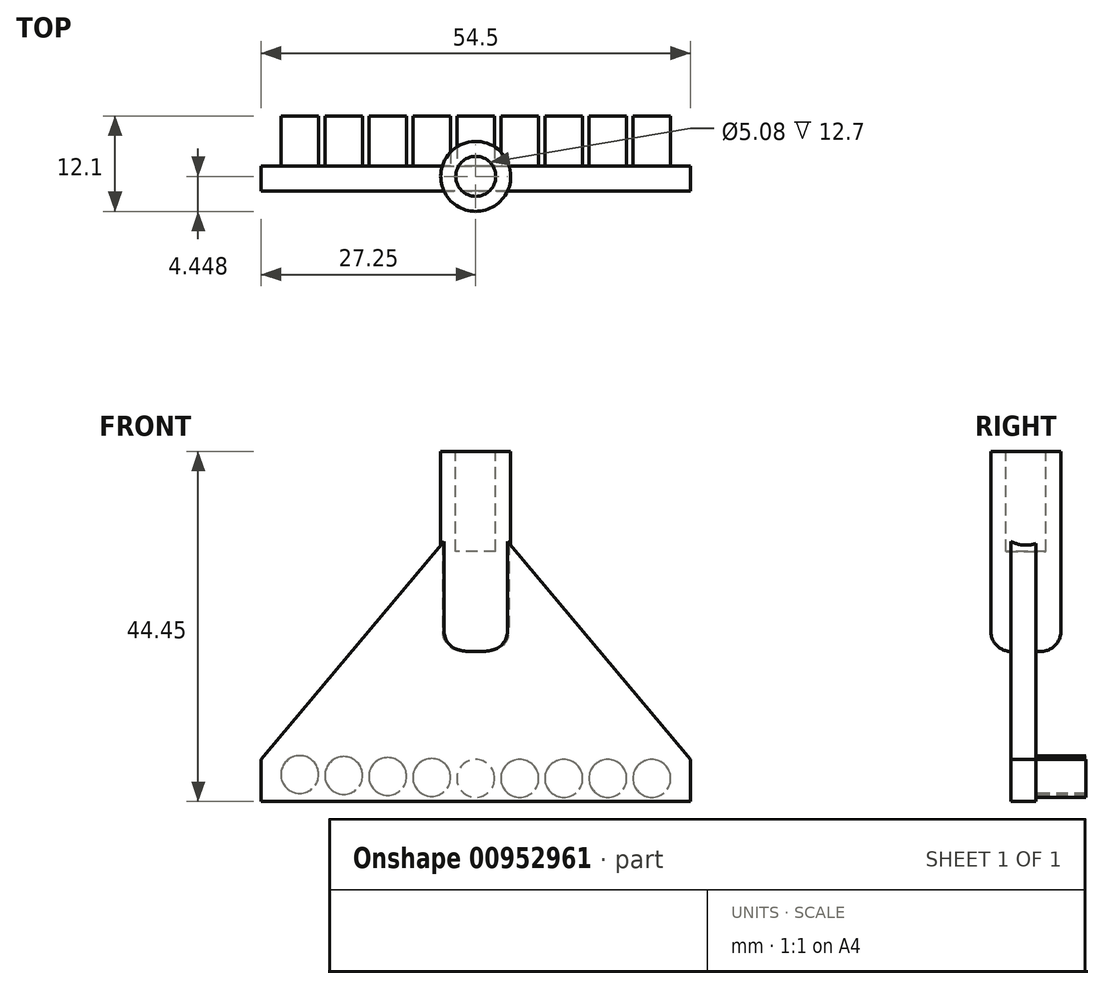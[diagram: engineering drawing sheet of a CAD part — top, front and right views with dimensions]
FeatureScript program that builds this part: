
annotation { "Feature Type Name" : "Feature", "Feature Type Description" : "" }
export const myFeature = defineFeature(function(context is Context, id is Id, definition is map)
    precondition{}
    {
        {
            var Q0;
            Q0=qCreatedBy(makeId("Front.planeOp"),FACE);
            var sketch = newSketch(context, id + "F0", { "sketchPlane" : qUnion([Q0])});
            skLineSegment(sketch, "E0", {"start": v(0, 37.84) * mm, "end": v(-27.25, 5.36) * mm});
            skLineSegment(sketch, "E1", {"start": v(-27.25, 0) * mm, "end": v(27.25, 0) * mm});
            skLineSegment(sketch, "E2", {"start": v(27.25, 5.36) * mm, "end": v(0, 37.84) * mm});
            skLineSegment(sketch, "E3", {"start": v(27.25, 5.36) * mm, "end": v(27.25, 0) * mm});
            skLineSegment(sketch, "E4.MirrorCS", {"start": v(-27.25, 5.36) * mm, "end": v(-27.25, 0) * mm});
            skPoint(sketch, "E5.orphan", {"position": v(31.75, 0) * mm});
            skPoint(sketch, "E6.orphan", {"position": v(-31.75, 0) * mm});
            skSolve(sketch);
        }
        {
            var Q0;
            Q0=makeQuery(id+"F0.imprint","IMPRINT",FACE,{"disambiguationData":[TD([[makeQuery(id+"F0.imprint","IMPRINT",EDGE,{"derivedFrom":sQuery(id+"F0.wireOp",EDGE,"E0")}),1.0]])]});
            extrude(context, id + "F1", {"entities" : qUnion([Q0]), "depth" : 3.17 * mm, "offsetDistance" : 25.4 * mm});
        }
        {
            var Q0;
            Q0=makeQuery(id+"F1.opExtrude","CAP_FACE",FACE,{"disambiguationData":[OSD([sQuery(id+"F0.wireOp",EDGE,"E0"),sQuery(id+"F0.wireOp",EDGE,"E1"),sQuery(id+"F0.wireOp",EDGE,"E2")])],"isStart":true});
            var sketch = newSketch(context, id + "F2", { "sketchPlane" : qUnion([Q0])});
            skCircle(sketch, "E7", {"center": v(0, 2.91) * mm, "radius": 2.4 * mm});
            skCircle(sketch, "E8.1.0.0", {"center": v(5.59, 3.04) * mm, "radius": 2.4 * mm});
            skCircle(sketch, "E8.2.0.0", {"center": v(11.18, 3.16) * mm, "radius": 2.4 * mm});
            skCircle(sketch, "E8.3.0.0", {"center": v(16.76, 3.28) * mm, "radius": 2.4 * mm});
            skCircle(sketch, "E8.4.0.0", {"center": v(22.35, 3.4) * mm, "radius": 2.4 * mm});
            skLineSegment(sketch, "E8.direction1", {"start": v(0, 2.91) * mm, "end": v(5.59, 3.04) * mm, "construction": true});
            skCircle(sketch, "E9.1.0.0", {"center": v(-5.59, 2.91) * mm, "radius": 2.4 * mm});
            skCircle(sketch, "E9.2.0.0", {"center": v(-11.18, 2.91) * mm, "radius": 2.4 * mm});
            skLineSegment(sketch, "E9.direction1", {"start": v(0, 2.91) * mm, "end": v(-5.59, 2.91) * mm, "construction": true});
            skCircle(sketch, "E10.0.3.0", {"center": v(-16.77, 2.91) * mm, "radius": 2.4 * mm});
            skCircle(sketch, "E10.0.4.0", {"center": v(-22.36, 2.91) * mm, "radius": 2.4 * mm});
            skSolve(sketch);
        }
        {
            var Q0;
            Q0=makeQuery(id+"F2.imprint","IMPRINT",FACE,{"disambiguationData":[TD([[makeQuery(id+"F2.imprint","IMPRINT",EDGE,{"derivedFrom":sQuery(id+"F2.wireOp",EDGE,"E8.3.0.0")}),1.0]])]});
            var Q1;
            Q1=makeQuery(id+"F2.imprint","IMPRINT",FACE,{"disambiguationData":[TD([[makeQuery(id+"F2.imprint","IMPRINT",EDGE,{"derivedFrom":sQuery(id+"F2.wireOp",EDGE,"E8.2.0.0")}),1.0]])]});
            var Q2;
            Q2=makeQuery(id+"F2.imprint","IMPRINT",FACE,{"disambiguationData":[TD([[makeQuery(id+"F2.imprint","IMPRINT",EDGE,{"derivedFrom":sQuery(id+"F2.wireOp",EDGE,"E8.1.0.0")}),1.0]])]});
            var Q3;
            Q3=makeQuery(id+"F2.imprint","IMPRINT",FACE,{"disambiguationData":[TD([[makeQuery(id+"F2.imprint","IMPRINT",EDGE,{"derivedFrom":sQuery(id+"F2.wireOp",EDGE,"E8.4.0.0")}),1.0]])]});
            var Q4;
            Q4=makeQuery(id+"F2.imprint","IMPRINT",FACE,{"disambiguationData":[TD([[makeQuery(id+"F2.imprint","IMPRINT",EDGE,{"derivedFrom":sQuery(id+"F2.wireOp",EDGE,"E7")}),1.0]])]});
            var Q5;
            Q5=makeQuery(id+"F2.imprint","IMPRINT",FACE,{"disambiguationData":[TD([[makeQuery(id+"F2.imprint","IMPRINT",EDGE,{"derivedFrom":sQuery(id+"F2.wireOp",EDGE,"E9.1.0.0")}),1.0]])]});
            var Q6;
            Q6=makeQuery(id+"F2.imprint","IMPRINT",FACE,{"disambiguationData":[TD([[makeQuery(id+"F2.imprint","IMPRINT",EDGE,{"derivedFrom":sQuery(id+"F2.wireOp",EDGE,"E9.2.0.0")}),1.0]])]});
            var Q7;
            Q7=makeQuery(id+"F2.imprint","IMPRINT",FACE,{"disambiguationData":[TD([[makeQuery(id+"F2.imprint","IMPRINT",EDGE,{"derivedFrom":sQuery(id+"F2.wireOp",EDGE,"E10.0.4.0")}),1.0]])]});
            var Q8;
            Q8=makeQuery(id+"F2.imprint","IMPRINT",FACE,{"disambiguationData":[TD([[makeQuery(id+"F2.imprint","IMPRINT",EDGE,{"derivedFrom":sQuery(id+"F2.wireOp",EDGE,"E10.0.3.0")}),1.0]])]});
            extrude(context, id + "F3", {"entities" : qUnion([Q0, Q1, Q2, Q3, Q4, Q5, Q6, Q7, Q8]), "operationType" : NewBodyOperationType.ADD, "depth" : 6.35 * mm, "offsetDistance" : 25.4 * mm});
        }
        {
            var Q0;
            Q0=qCreatedBy(makeId("Top.planeOp"),FACE);
            cPlane(context, id + "F4", {"entities" : qUnion([Q0]), "cplaneType" : CPlaneType.OFFSET, "offset" : 19.05 * mm, "width" : 152.4 * mm, "height" : 152.4 * mm});
        }
        {
            var Q0;
            Q0=qCreatedBy(id+"F4.planeOp",FACE);
            var sketch = newSketch(context, id + "F5", { "sketchPlane" : qUnion([Q0])});
            skCircle(sketch, "E11", {"center": v(0, -1.3) * mm, "radius": 4.45 * mm});
            skSolve(sketch);
        }
        {
            var Q0;
            Q0=makeQuery(id+"F5.imprint","IMPRINT",FACE,{"disambiguationData":[TD([[makeQuery(id+"F5.imprint","IMPRINT",EDGE,{"derivedFrom":sQuery(id+"F5.wireOp",EDGE,"E11")}),1.0]])]});
            extrude(context, id + "F6", {"entities" : qUnion([Q0]), "operationType" : NewBodyOperationType.ADD, "depth" : 25.4 * mm, "offsetDistance" : 25.4 * mm});
        }
        {
            var Q0;
            {var subQ0=sQuery(id+"F5.wireOp",EDGE,"E11");Q0=makeQuery(id+"F6.boolean.opBoolean","SPLIT",EDGE,{"disambiguationData":[TD([makeQuery(id+"F1.opExtrude","CAP_FACE",FACE,{"disambiguationData":[OSD([sQuery(id+"F0.wireOp",EDGE,"E0"),sQuery(id+"F0.wireOp",EDGE,"E1"),sQuery(id+"F0.wireOp",EDGE,"E2"),sQuery(id+"F0.wireOp",EDGE,"E3"),sQuery(id+"F0.wireOp",EDGE,"E4.MirrorCS")])],"isStart":true})])],"derivedFrom":makeQuery(id+"F6.opExtrude","CAP_EDGE",EDGE,{"disambiguationData":[OSD([subQ0])],"isStart":true})});}
            fillet(context, id + "F7", {"entities" : qUnion([Q0]), "radius" : 2.54 * mm, "allowEdgeOverflow" : false});
        }
        {
            var Q0;
            {var subQ0=sQuery(id+"F5.wireOp",EDGE,"E11");Q0=makeQuery(id+"F6.boolean.opBoolean","SPLIT",EDGE,{"disambiguationData":[TD([makeQuery(id+"F1.opExtrude","CAP_FACE",FACE,{"disambiguationData":[OSD([sQuery(id+"F0.wireOp",EDGE,"E0"),sQuery(id+"F0.wireOp",EDGE,"E1"),sQuery(id+"F0.wireOp",EDGE,"E2"),sQuery(id+"F0.wireOp",EDGE,"E3"),sQuery(id+"F0.wireOp",EDGE,"E4.MirrorCS")])],"isStart":false})])],"derivedFrom":makeQuery(id+"F6.opExtrude","CAP_EDGE",EDGE,{"disambiguationData":[OSD([subQ0])],"isStart":true})});}
            fillet(context, id + "F8", {"entities" : qUnion([Q0]), "radius" : 2.54 * mm, "allowEdgeOverflow" : false});
        }
        {
            var Q0;
            Q0=makeQuery(id+"F6.opExtrude","CAP_FACE",FACE,{"disambiguationData":[OSD([sQuery(id+"F5.wireOp",EDGE,"E11")])],"isStart":false});
            var sketch = newSketch(context, id + "F9", { "sketchPlane" : qUnion([Q0])});
            skCircle(sketch, "E12", {"center": v(0, -1.3) * mm, "radius": 2.54 * mm});
            skSolve(sketch);
        }
        {
            var Q0;
            Q0=makeQuery(id+"F9.imprint","IMPRINT",FACE,{"disambiguationData":[TD([[makeQuery(id+"F9.imprint","IMPRINT",EDGE,{"derivedFrom":sQuery(id+"F9.wireOp",EDGE,"E12")}),1.0]])]});
            extrude(context, id + "F10", {"entities" : qUnion([Q0]), "operationType" : NewBodyOperationType.REMOVE, "oppositeDirection" : true, "depth" : 12.7 * mm, "offsetDistance" : 25.4 * mm});
        }
    });
